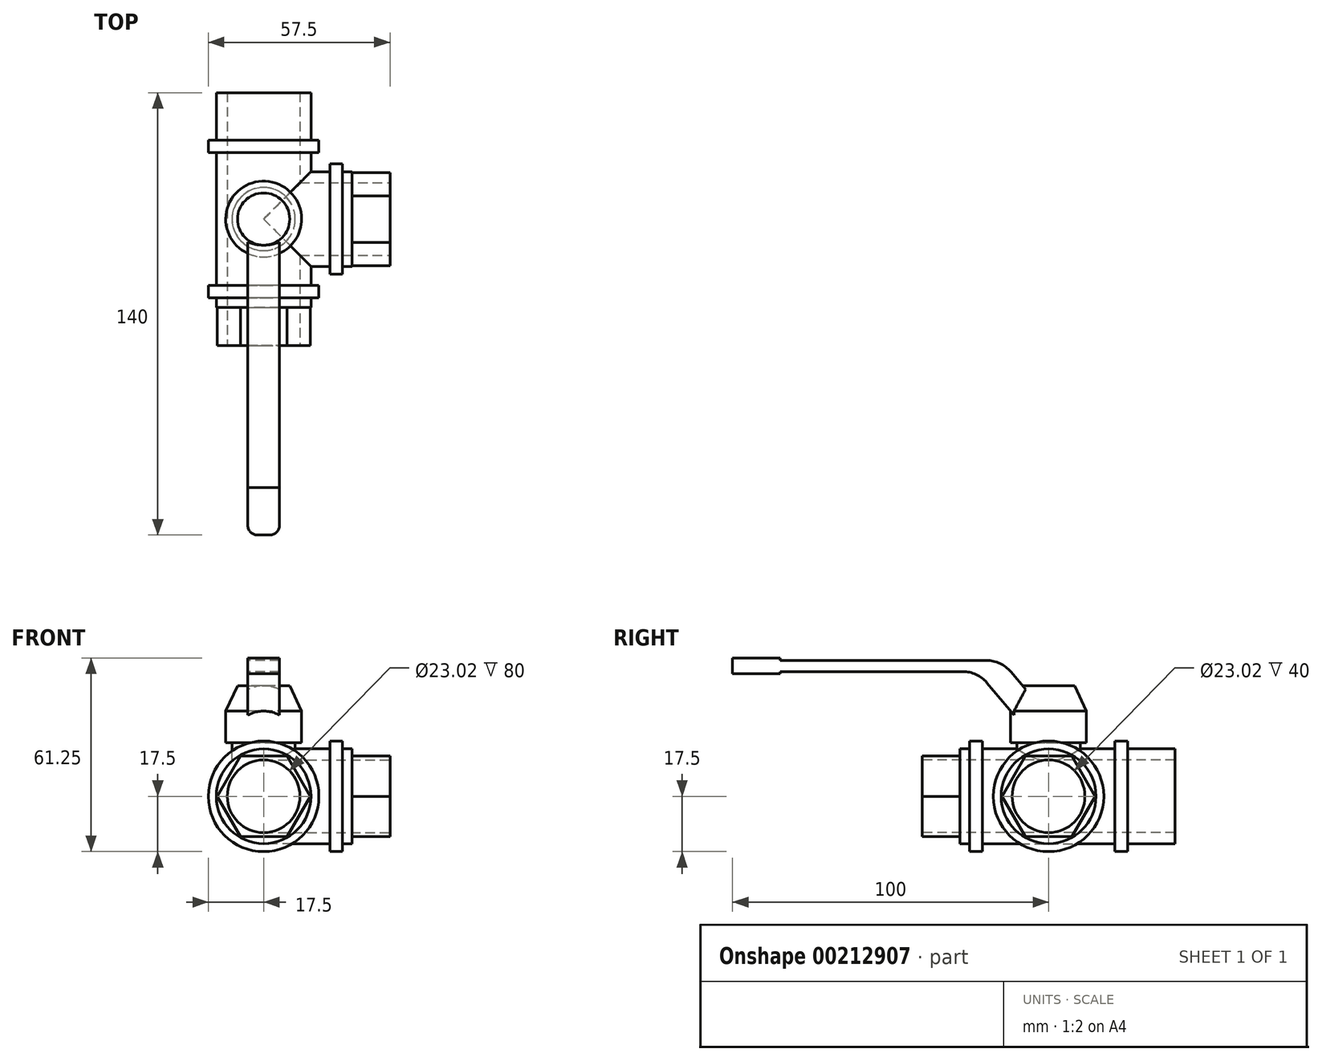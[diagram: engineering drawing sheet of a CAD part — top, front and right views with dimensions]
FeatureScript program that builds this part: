
annotation { "Feature Type Name" : "Feature", "Feature Type Description" : "" }
export const myFeature = defineFeature(function(context is Context, id is Id, definition is map)
    precondition{}
    {
        {
            var Q0;
            Q0=qCreatedBy(makeId("Front.planeOp"),FACE);
            var sketch = newSketch(context, id + "F0", { "sketchPlane" : qUnion([Q0])});
            skCircle(sketch, "E0", {"center": v(0, 0) * mm, "radius": 15 * mm});
            skSolve(sketch);
        }
        {
            var Q0;
            Q0=makeQuery(id+"F0.imprint","IMPRINT",FACE,{"disambiguationData":[TD([[makeQuery(id+"F0.imprint","IMPRINT",EDGE,{"derivedFrom":sQuery(id+"F0.wireOp",EDGE,"E0")}),1.0]])]});
            extrude(context, id + "F1", {"entities" : qUnion([Q0]), "endBound" : BoundingType.SYMMETRIC, "depth" : 80 * mm});
        }
        {
            var Q0;
            Q0=qCreatedBy(makeId("Right.planeOp"),FACE);
            var sketch = newSketch(context, id + "F2", { "sketchPlane" : qUnion([Q0])});
            skCircle(sketch, "E1", {"center": v(0, 0) * mm, "radius": 15 * mm});
            skSolve(sketch);
        }
        {
            var Q0;
            Q0 = qSketchRegion(id + "F2", true);
            extrude(context, id + "F3", {"entities" : qUnion([Q0]), "operationType" : NewBodyOperationType.ADD, "depth" : 40 * mm});
        }
        {
            var Q0;
            Q0=qCreatedBy(makeId("Right.planeOp"),FACE);
            var sketch = newSketch(context, id + "F4", { "sketchPlane" : qUnion([Q0])});
            skLineSegment(sketch, "E2", {"start": v(10, 0) * mm, "end": v(10, 17) * mm});
            skLineSegment(sketch, "E3", {"start": v(10, 17) * mm, "end": v(12, 17) * mm});
            skLineSegment(sketch, "E4", {"start": v(12, 17) * mm, "end": v(12, 27) * mm});
            skLineSegment(sketch, "E5", {"start": v(12, 27) * mm, "end": v(8.27, 35) * mm});
            skLineSegment(sketch, "E6", {"start": v(8.27, 35) * mm, "end": v(0, 35) * mm});
            skLineSegment(sketch, "E7", {"start": v(0, 35) * mm, "end": v(0, 0) * mm});
            skLineSegment(sketch, "E8", {"start": v(0, 0) * mm, "end": v(10, 0) * mm});
            skLineSegment(sketch, "E9", {"start": v(0, 15) * mm, "end": v(40, 15) * mm, "construction": true});
            skSolve(sketch);
        }
        {
            var Q0;
            Q0 = qSketchRegion(id + "F4", true);
            var Q1;
            Q1=sQuery(id+"F4.wireOp",EDGE,"E7");
            revolve(context, id + "F5", {"operationType" : NewBodyOperationType.ADD, "entities" : qUnion([Q0]), "axis" : qUnion([Q1]), "revolveType" : RevolveType.FULL});
        }
        {
            var Q0;
            Q0=qCreatedBy(makeId("Right.planeOp"),FACE);
            var sketch = newSketch(context, id + "F6", { "sketchPlane" : qUnion([Q0])});
            skLineSegment(sketch, "E10", {"start": v(0, 25.14) * mm, "end": v(-14.98, 43) * mm});
            skLineSegment(sketch, "E11", {"start": v(-14.98, 43) * mm, "end": v(-85, 43) * mm});
            skLineSegment(sketch, "E12", {"start": v(-85, 43) * mm, "end": v(-85, 43.75) * mm});
            skLineSegment(sketch, "E13", {"start": v(-85, 43.75) * mm, "end": v(-100, 43.75) * mm});
            skLineSegment(sketch, "E14", {"start": v(-100, 43.75) * mm, "end": v(-100, 38.75) * mm});
            skLineSegment(sketch, "E15", {"start": v(-100, 38.75) * mm, "end": v(-85, 38.75) * mm});
            skLineSegment(sketch, "E16", {"start": v(-85, 38.75) * mm, "end": v(-85, 39.5) * mm});
            skLineSegment(sketch, "E17", {"start": v(-85, 39.5) * mm, "end": v(-22.49, 39.5) * mm});
            skLineSegment(sketch, "E18", {"start": v(-22.49, 39.5) * mm, "end": v(0, 12.7) * mm});
            skLineSegment(sketch, "E19", {"start": v(0, 12.7) * mm, "end": v(0, 25.14) * mm});
            skLineSegment(sketch, "E20", {"start": v(-12, 17) * mm, "end": v(-12, 27) * mm});
            skLineSegment(sketch, "E21", {"start": v(-12, 27) * mm, "end": v(-8.27, 35) * mm});
            skSolve(sketch);
        }
        {
            var Q0;
            Q0 = qSketchRegion(id + "F6", true);
            extrude(context, id + "F7", {"entities" : qUnion([Q0]), "operationType" : NewBodyOperationType.ADD, "endBound" : BoundingType.SYMMETRIC, "depth" : 10 * mm});
        }
        {
            var Q0;
            Q0=makeQuery(id+"F7.opExtrude","CAP_EDGE",EDGE,{"disambiguationData":[OSD([sQuery(id+"F6.wireOp",EDGE,"E14")])],"isStart":true});
            var Q1;
            Q1=makeQuery(id+"F7.opExtrude","CAP_EDGE",EDGE,{"disambiguationData":[OSD([sQuery(id+"F6.wireOp",EDGE,"E14")])],"isStart":false});
            fillet(context, id + "F8", {"entities" : qUnion([Q0, Q1]), "radius" : 3 * mm, "tangentPropagation" : true, "allowEdgeOverflow" : false});
        }
        {
            var Q0;
            Q0=makeQuery(id+"F7.opExtrude","SWEPT_EDGE",EDGE,{"disambiguationData":[OSD([sQuery(id+"F6.wireOp",EDGE,"E17"),sQuery(id+"F6.wireOp",EDGE,"E18")])]});
            var Q1;
            Q1=makeQuery(id+"F7.opExtrude","SWEPT_EDGE",EDGE,{"disambiguationData":[OSD([sQuery(id+"F6.wireOp",EDGE,"E10"),sQuery(id+"F6.wireOp",EDGE,"E11")])]});
            fillet(context, id + "F9", {"entities" : qUnion([Q0, Q1]), "radius" : 10 * mm, "tangentPropagation" : true, "allowEdgeOverflow" : false});
        }
        {
            var Q0;
            Q0=qCreatedBy(makeId("Right.planeOp"),FACE);
            var sketch = newSketch(context, id + "F10", { "sketchPlane" : qUnion([Q0])});
            skLineSegment(sketch, "E22.0", {"start": v(40, -15) * mm, "end": v(40, 15) * mm, "construction": true});
            skLineSegment(sketch, "E23.0", {"start": v(-40, -15) * mm, "end": v(-40, 15) * mm, "construction": true});
            skLineSegment(sketch, "E24", {"start": v(40, 0) * mm, "end": v(-40, 0) * mm, "construction": true});
            skLineSegment(sketch, "E25.bottom", {"start": v(25, 0) * mm, "end": v(21, 0) * mm});
            skLineSegment(sketch, "E25.top", {"start": v(25, 17.5) * mm, "end": v(21, 17.5) * mm});
            skLineSegment(sketch, "E25.left", {"start": v(25, 0) * mm, "end": v(25, 17.5) * mm});
            skLineSegment(sketch, "E25.right", {"start": v(21, 0) * mm, "end": v(21, 17.5) * mm});
            skLineSegment(sketch, "E26.bottom", {"start": v(-21, 0) * mm, "end": v(-25, 0) * mm});
            skLineSegment(sketch, "E26.top", {"start": v(-21, 17.5) * mm, "end": v(-25, 17.5) * mm});
            skLineSegment(sketch, "E26.left", {"start": v(-21, 0) * mm, "end": v(-21, 17.5) * mm});
            skLineSegment(sketch, "E26.right", {"start": v(-25, 0) * mm, "end": v(-25, 17.5) * mm});
            skLineSegment(sketch, "E27", {"start": v(21, 17.5) * mm, "end": v(-21, 17.5) * mm, "construction": true});
            skPoint(sketch, "E28", {"position": v(0, 17.5) * mm});
            skSolve(sketch);
        }
        {
            var Q0;
            Q0 = qSketchRegion(id + "F10", true);
            var Q1;
            Q1=sQuery(id+"F10.wireOp",EDGE,"E24");
            revolve(context, id + "F11", {"operationType" : NewBodyOperationType.ADD, "entities" : qUnion([Q0]), "axis" : qUnion([Q1]), "revolveType" : RevolveType.FULL});
        }
        {
            var Q0;
            Q0=qCreatedBy(makeId("Right.planeOp"),FACE);
            cPlane(context, id + "F12", {"entities" : qUnion([Q0]), "cplaneType" : CPlaneType.OFFSET, "offset" : 25 * mm, "width" : 150 * mm, "height" : 150 * mm});
        }
        {
            var Q0;
            Q0=qCreatedBy(id+"F12.planeOp",FACE);
            var sketch = newSketch(context, id + "F13", { "sketchPlane" : qUnion([Q0])});
            skCircle(sketch, "E29", {"center": v(0, 0) * mm, "radius": 17.5 * mm});
            skSolve(sketch);
        }
        {
            var Q0;
            Q0 = qSketchRegion(id + "F13", true);
            extrude(context, id + "F14", {"entities" : qUnion([Q0]), "operationType" : NewBodyOperationType.ADD, "oppositeDirection" : true, "depth" : 4 * mm});
        }
        {
            var Q0;
            Q0=makeQuery(id+"F1.opExtrude","CAP_FACE",FACE,{"disambiguationData":[OSD([sQuery(id+"F0.wireOp",EDGE,"E0")])],"isStart":false});
            var sketch = newSketch(context, id + "F15", { "sketchPlane" : qUnion([Q0])});
            skCircle(sketch, "E30.0", {"center": v(0, 0) * mm, "radius": 15 * mm});
            skCircle(sketch, "E31.cCircle", {"center": v(0, 0) * mm, "radius": 12.75 * mm, "construction": true});
            skLineSegment(sketch, "E31.0", {"start": v(-7.36, 12.75) * mm, "end": v(7.36, 12.75) * mm});
            skLineSegment(sketch, "E31.1", {"start": v(7.36, 12.75) * mm, "end": v(14.72, 0) * mm});
            skLineSegment(sketch, "E31.2", {"start": v(14.72, 0) * mm, "end": v(7.36, -12.75) * mm});
            skLineSegment(sketch, "E31.3", {"start": v(7.36, -12.75) * mm, "end": v(-7.36, -12.75) * mm});
            skLineSegment(sketch, "E31.4", {"start": v(-7.36, -12.75) * mm, "end": v(-14.72, 0) * mm});
            skLineSegment(sketch, "E31.5", {"start": v(-14.72, 0) * mm, "end": v(-7.36, 12.75) * mm});
            skPoint(sketch, "E31.0.midPoint", {"position": v(0, 12.75) * mm});
            skSolve(sketch);
        }
        {
            var Q0;
            Q0 = qSketchRegion(id + "F15", true);
            var Q1;
            Q1=makeQuery(id+"F11.opRevolve","SWEPT_FACE",FACE,{"disambiguationData":[OSD([sQuery(id+"F10.wireOp",EDGE,"E26.right")])]});
            extrude(context, id + "F16", {"entities" : qUnion([Q0]), "operationType" : NewBodyOperationType.REMOVE, "oppositeDirection" : true, "endBoundEntityFace" : qUnion([Q1]), "depth" : 12 * mm});
        }
        {
            var Q0;
            Q0=makeQuery(id+"F1.opExtrude","CAP_FACE",FACE,{"disambiguationData":[OSD([sQuery(id+"F0.wireOp",EDGE,"E0")])],"isStart":false});
            var sketch = newSketch(context, id + "F17", { "sketchPlane" : qUnion([Q0])});
            skPoint(sketch, "E32", {"position": v(0, 0) * mm});
            skSolve(sketch);
        }
        {
            var Q0;
            Q0=sQuery(id+"F17.wireOp",VERTEX,"E32");
            var Q1;
            Q1=makeQuery(id+"F1.opExtrude","SWEPT_BODY",BODY,{"disambiguationData":[OSD([sQuery(id+"F0.wireOp",EDGE,"E0")])]});
            hole(context, id + "F18", {"style" : HoleStyle.SIMPLE, "endStyle" : HoleEndStyle.THROUGH, "standardTappedOrClearance" : lookupTablePath({ "standard" : "ANSI", "fit" : "Normal (ASME)", "size" : "7/8", "type" : "Clearance" }), "standardBlindInLast" : lookupTablePath({ "fit" : "Free", "standard" : "ANSI", "size" : "7/8", "type" : "Clearance" }), "holeDiameter" : 23.02 * mm, "locations" : qUnion([Q0]), "scope" : qUnion([Q1]), "isTappedThrough" : true});
        }
        {
            var Q0;
            Q0=makeQuery(id+"F3.opExtrude","CAP_FACE",FACE,{"disambiguationData":[OSD([sQuery(id+"F2.wireOp",EDGE,"E1")])],"isStart":false});
            var sketch = newSketch(context, id + "F19", { "sketchPlane" : qUnion([Q0])});
            skCircle(sketch, "E33.0", {"center": v(0, 0) * mm, "radius": 15 * mm});
            skCircle(sketch, "E34.cCircle", {"center": v(0, 0) * mm, "radius": 12.75 * mm, "construction": true});
            skLineSegment(sketch, "E34.0", {"start": v(-7.36, 12.75) * mm, "end": v(7.36, 12.75) * mm});
            skLineSegment(sketch, "E34.1", {"start": v(7.36, 12.75) * mm, "end": v(14.72, 0) * mm});
            skLineSegment(sketch, "E34.2", {"start": v(14.72, 0) * mm, "end": v(7.36, -12.75) * mm});
            skLineSegment(sketch, "E34.3", {"start": v(7.36, -12.75) * mm, "end": v(-7.36, -12.75) * mm});
            skLineSegment(sketch, "E34.4", {"start": v(-7.36, -12.75) * mm, "end": v(-14.72, 0) * mm});
            skLineSegment(sketch, "E34.5", {"start": v(-14.72, 0) * mm, "end": v(-7.36, 12.75) * mm});
            skPoint(sketch, "E34.0.midPoint", {"position": v(0, 12.75) * mm});
            skSolve(sketch);
        }
        {
            var Q0;
            Q0 = qSketchRegion(id + "F19", true);
            extrude(context, id + "F20", {"entities" : qUnion([Q0]), "operationType" : NewBodyOperationType.REMOVE, "oppositeDirection" : true, "depth" : 12 * mm});
        }
        {
            var Q0;
            Q0=makeQuery(id+"F3.opExtrude","CAP_FACE",FACE,{"disambiguationData":[OSD([sQuery(id+"F2.wireOp",EDGE,"E1")])],"isStart":false});
            var sketch = newSketch(context, id + "F21", { "sketchPlane" : qUnion([Q0])});
            skPoint(sketch, "E35", {"position": v(0, 0) * mm});
            skSolve(sketch);
        }
        {
            var Q0;
            Q0=sQuery(id+"F21.wireOp",VERTEX,"E35");
            var Q1;
            Q1=makeQuery(id+"F1.opExtrude","SWEPT_BODY",BODY,{"disambiguationData":[OSD([sQuery(id+"F0.wireOp",EDGE,"E0")])]});
            hole(context, id + "F22", {"style" : HoleStyle.SIMPLE, "endStyle" : HoleEndStyle.BLIND, "standardTappedOrClearance" : lookupTablePath({ "standard" : "ANSI", "fit" : "Normal (ASME)", "size" : "7/8", "type" : "Clearance" }), "standardBlindInLast" : lookupTablePath({ "fit" : "Free", "standard" : "ANSI", "size" : "7/8", "type" : "Clearance" }), "holeDiameter" : 23.02 * mm, "holeDepth" : 40 * mm, "locations" : qUnion([Q0]), "scope" : qUnion([Q1])});
        }
    });
